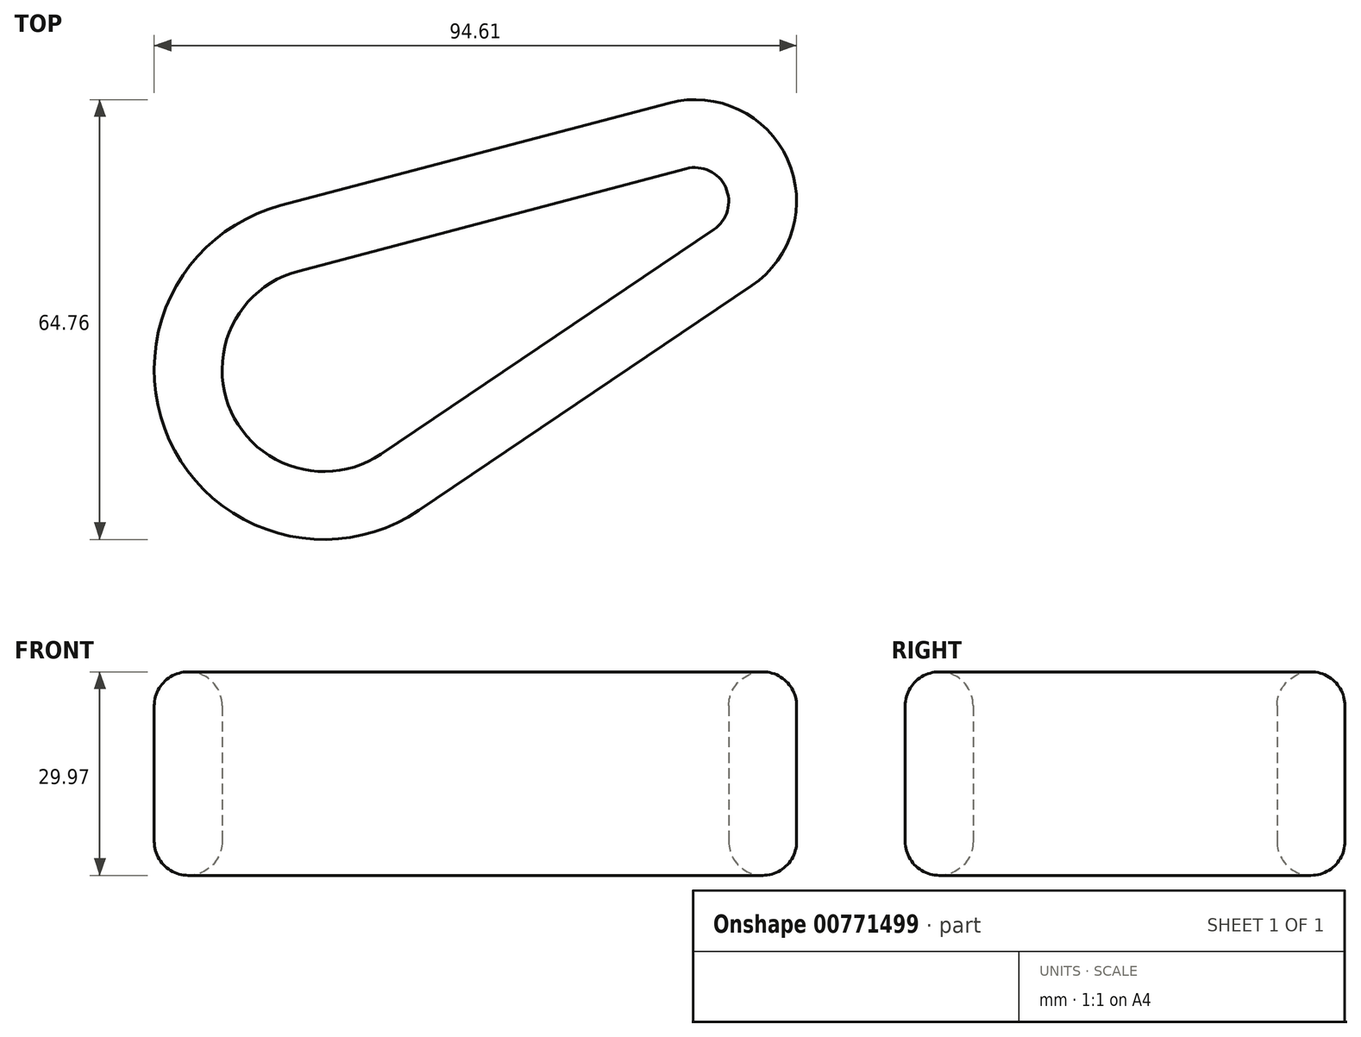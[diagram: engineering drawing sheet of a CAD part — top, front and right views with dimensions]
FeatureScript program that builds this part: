
annotation { "Feature Type Name" : "Feature", "Feature Type Description" : "" }
export const myFeature = defineFeature(function(context is Context, id is Id, definition is map)
    precondition{}
    {
        {
            var Q0;
            Q0=qCreatedBy(makeId("Top.planeOp"),FACE);
            var sketch = newSketch(context, id + "F0", { "sketchPlane" : qUnion([Q0])});
            skArc(sketch, "E0", {"start": v(-6.38, 24.17) * mm, "mid": v(-22.76, -10.32) * mm, "end": v(13.98, -20.72) * mm});
            skArc(sketch, "E1", {"start": v(63.02, 12.36) * mm, "mid": v(68.29, 30.97) * mm, "end": v(50.81, 39.27) * mm});
            skLineSegment(sketch, "E2", {"start": v(-6.38, 24.17) * mm, "end": v(50.81, 39.27) * mm});
            skLineSegment(sketch, "E3", {"start": v(54.64, 24.78) * mm, "end": v(0, 0) * mm, "construction": true});
            skLineSegment(sketch, "E4.MirrorCS", {"start": v(13.98, -20.72) * mm, "end": v(63.02, 12.36) * mm});
            skArc(sketch, "E5.0", {"start": v(-3.83, 14.5) * mm, "mid": v(-13.65, -6.2) * mm, "end": v(8.38, -12.43) * mm});
            skLineSegment(sketch, "E6.0", {"start": v(8.38, -12.43) * mm, "end": v(57.43, 20.65) * mm});
            skLineSegment(sketch, "E7.0", {"start": v(-3.83, 14.5) * mm, "end": v(53.36, 29.6) * mm});
            skArc(sketch, "E8.0", {"start": v(57.43, 20.65) * mm, "mid": v(59.18, 26.84) * mm, "end": v(53.36, 29.6) * mm});
            skSolve(sketch);
        }
        {
            var Q0;
            Q0 = qSketchRegion(id + "F0", true);
            extrude(context, id + "F1", {"entities" : qUnion([Q0]), "depth" : 29.97 * mm, "offsetDistance" : 25.4 * mm});
        }
        {
            var Q0;
            Q0=makeQuery(id+"F1.opExtrude","CAP_FACE",FACE,{"disambiguationData":[OSD([sQuery(id+"F0.wireOp",EDGE,"E0"),sQuery(id+"F0.wireOp",EDGE,"E1"),sQuery(id+"F0.wireOp",EDGE,"E2"),sQuery(id+"F0.wireOp",EDGE,"E4.MirrorCS"),sQuery(id+"F0.wireOp",EDGE,"E5.0"),sQuery(id+"F0.wireOp",EDGE,"E6.0"),sQuery(id+"F0.wireOp",EDGE,"E7.0"),sQuery(id+"F0.wireOp",EDGE,"E8.0")])],"isStart":false});
            var Q1;
            Q1=makeQuery(id+"F1.opExtrude","CAP_FACE",FACE,{"disambiguationData":[OSD([sQuery(id+"F0.wireOp",EDGE,"E0"),sQuery(id+"F0.wireOp",EDGE,"E1"),sQuery(id+"F0.wireOp",EDGE,"E2"),sQuery(id+"F0.wireOp",EDGE,"E4.MirrorCS"),sQuery(id+"F0.wireOp",EDGE,"E5.0"),sQuery(id+"F0.wireOp",EDGE,"E6.0"),sQuery(id+"F0.wireOp",EDGE,"E7.0"),sQuery(id+"F0.wireOp",EDGE,"E8.0")])],"isStart":true});
            fillet(context, id + "F2", {"entities" : qUnion([Q0, Q1]), "radius" : 5 * mm, "tangentPropagation" : true, "allowEdgeOverflow" : false});
        }
    });
